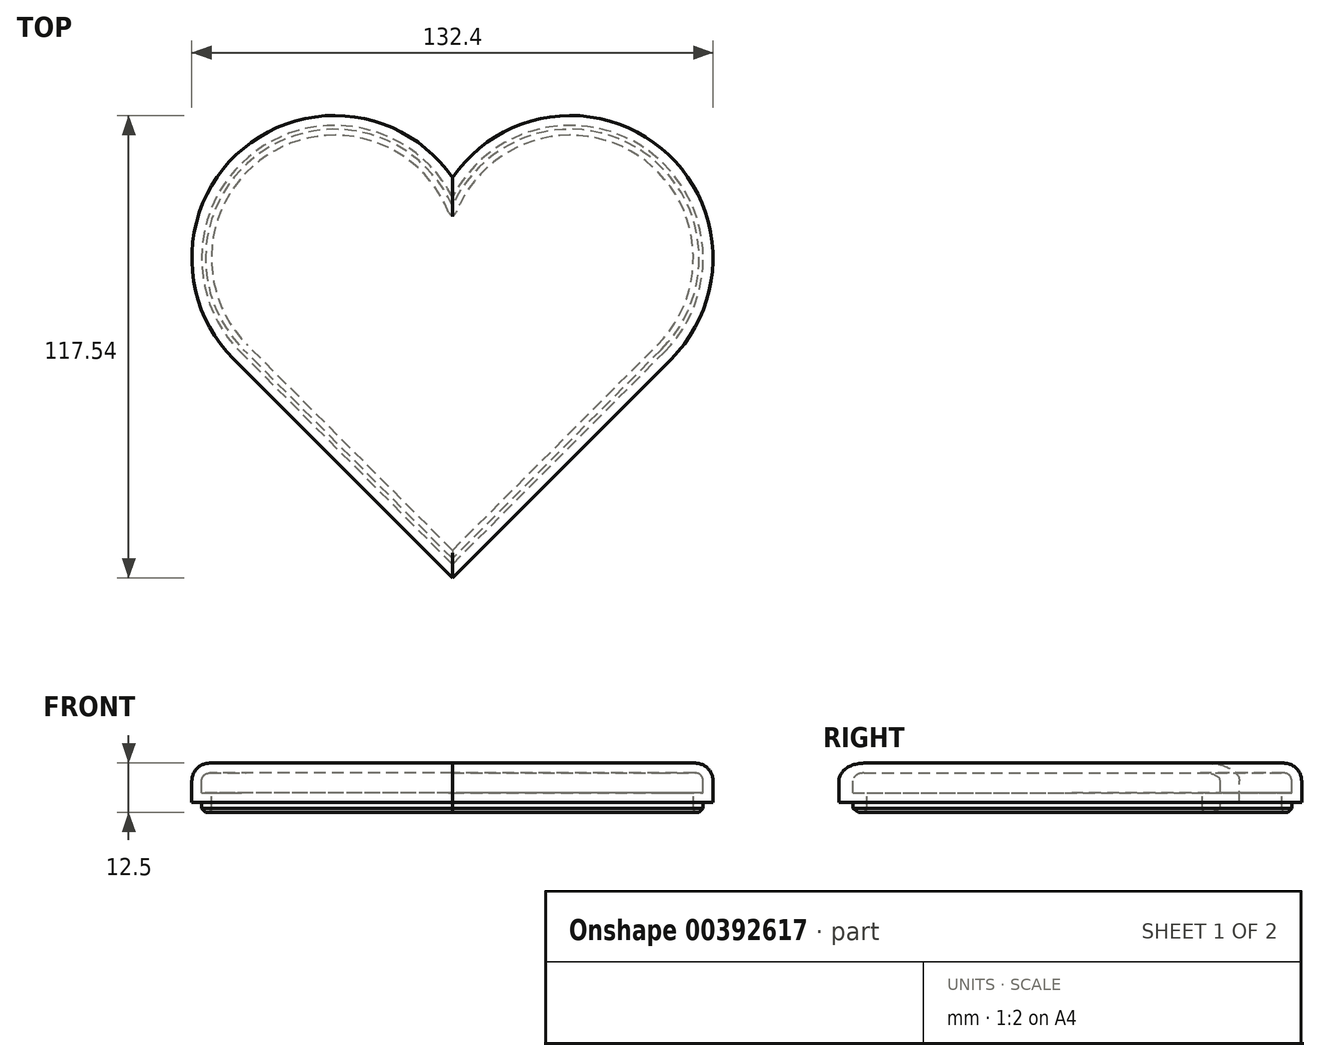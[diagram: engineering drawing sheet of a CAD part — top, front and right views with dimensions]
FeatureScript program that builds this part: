
annotation { "Feature Type Name" : "Feature", "Feature Type Description" : "" }
export const myFeature = defineFeature(function(context is Context, id is Id, definition is map)
    precondition{}
    {
        {
            var Q0;
            Q0=qCreatedBy(makeId("Top.planeOp"),FACE);
            var sketch = newSketch(context, id + "F0", { "sketchPlane" : qUnion([Q0])});
            skLineSegment(sketch, "E0", {"start": v(0, -53.9) * mm, "end": v(53.83, 0) * mm});
            skArc(sketch, "E1", {"start": v(53.83, 0) * mm, "mid": v(49.9, 51.09) * mm, "end": v(0, 39.44) * mm});
            skLineSegment(sketch, "E2", {"start": v(0, -53.9) * mm, "end": v(-53.83, 0) * mm});
            skArc(sketch, "E3", {"start": v(-53.83, 0) * mm, "mid": v(-49.9, 51.09) * mm, "end": v(0, 39.44) * mm});
            skSolve(sketch);
        }
        {
            var Q0;
            Q0=makeQuery(id+"F0.imprint","IMPRINT",FACE,{"disambiguationData":[TD([[makeQuery(id+"F0.imprint","IMPRINT",EDGE,{"derivedFrom":sQuery(id+"F0.wireOp",EDGE,"E0")}),1.0]])]});
            extrude(context, id + "F1", {"entities" : qUnion([Q0]), "oppositeDirection" : true, "depth" : 5 * mm});
        }
        {
            var Q0;
            Q0=makeQuery(id+"F1.opExtrude","CAP_EDGE",EDGE,{"disambiguationData":[OSD([sQuery(id+"F0.wireOp",EDGE,"E0")])],"isStart":true});
            var Q1;
            Q1=makeQuery(id+"F1.opExtrude","CAP_EDGE",EDGE,{"disambiguationData":[OSD([sQuery(id+"F0.wireOp",EDGE,"E2")])],"isStart":true});
            var Q2;
            Q2=makeQuery(id+"F1.opExtrude","CAP_EDGE",EDGE,{"disambiguationData":[OSD([sQuery(id+"F0.wireOp",EDGE,"E3")])],"isStart":true});
            var Q3;
            Q3=makeQuery(id+"F1.opExtrude","CAP_EDGE",EDGE,{"disambiguationData":[OSD([sQuery(id+"F0.wireOp",EDGE,"E1")])],"isStart":true});
            fillet(context, id + "F2", {"entities" : qUnion([Q0, Q1, Q2, Q3]), "radius" : 2 * mm, "tangentPropagation" : true, "allowEdgeOverflow" : false});
        }
        {
            var Q0;
            Q0=makeQuery(id+"F1.opExtrude","CAP_FACE",FACE,{"disambiguationData":[OSD([sQuery(id+"F0.wireOp",EDGE,"E0"),sQuery(id+"F0.wireOp",EDGE,"E1"),sQuery(id+"F0.wireOp",EDGE,"E2"),sQuery(id+"F0.wireOp",EDGE,"E3")])],"isStart":false});
            shell(context, id + "F3", {"entities" : qUnion([Q0]), "thickness" : 2.5 * mm});
        }
        {
            var Q0;
            Q0=makeQuery(id+"F3.opShell","OFFSET_FACE",FACE,{"disambiguationData":[OSD([sQuery(id+"F0.wireOp",EDGE,"E0"),sQuery(id+"F0.wireOp",EDGE,"E1"),sQuery(id+"F0.wireOp",EDGE,"E2"),sQuery(id+"F0.wireOp",EDGE,"E3")])]});
            extrude(context, id + "F4", {"entities" : qUnion([Q0]), "operationType" : NewBodyOperationType.ADD, "depth" : 7.5 * mm});
        }
        {
            var Q0;
            {var subQ0=sQuery(id+"F0.wireOp",EDGE,"E2");var subQ1=makeQuery(id+"F1.opExtrude","CAP_EDGE",EDGE,{"disambiguationData":[OSD([subQ0])],"isStart":true});var subQ2=sQuery(id+"F0.wireOp",EDGE,"E3");var subQ3=sQuery(id+"F0.wireOp",EDGE,"E1");var subQ4=sQuery(id+"F0.wireOp",EDGE,"E0");Q0=makeQuery(id+"F4.opExtrude","CAP_EDGE",EDGE,{"disambiguationData":[OSD([subQ4,subQ3,subQ0,subQ2]),TDD([makeQuery(id+"F3.opShell","OFFSET_EDGE",EDGE,{"disambiguationData":[OSD([subQ4,subQ3,subQ0,subQ2]),TDD([makeQuery(id+"F2.opFillet","BLEND_EDGE",EDGE,{"blendedFrom":[subQ1,makeQuery(id+"F1.opExtrude","CAP_FACE",FACE,{"disambiguationData":[OSD([subQ4,subQ3,subQ0,subQ2])],"isStart":true})],"blendedInto":[makeQuery(id+"F1.opExtrude","CAP_FACE",FACE,{"disambiguationData":[OSD([subQ4,subQ3,subQ0,subQ2])],"isStart":true})]}),makeQuery(id+"F2.opFillet","BLEND_EDGE",EDGE,{"blendedFrom":[subQ1,makeQuery(id+"F1.opExtrude","SWEPT_FACE",FACE,{"disambiguationData":[OSD([subQ0])]})],"blendedInto":[makeQuery(id+"F1.opExtrude","SWEPT_FACE",FACE,{"disambiguationData":[OSD([subQ0])]})]})])]})])],"isStart":false});}
            var Q1;
            {var subQ0=sQuery(id+"F0.wireOp",EDGE,"E3");var subQ1=makeQuery(id+"F1.opExtrude","CAP_EDGE",EDGE,{"disambiguationData":[OSD([subQ0])],"isStart":true});var subQ2=sQuery(id+"F0.wireOp",EDGE,"E2");var subQ3=sQuery(id+"F0.wireOp",EDGE,"E1");var subQ4=sQuery(id+"F0.wireOp",EDGE,"E0");Q1=makeQuery(id+"F4.opExtrude","CAP_EDGE",EDGE,{"disambiguationData":[OSD([subQ4,subQ3,subQ2,subQ0]),TDD([makeQuery(id+"F3.opShell","OFFSET_EDGE",EDGE,{"disambiguationData":[OSD([subQ4,subQ3,subQ2,subQ0]),TDD([makeQuery(id+"F2.opFillet","BLEND_EDGE",EDGE,{"blendedFrom":[subQ1,makeQuery(id+"F1.opExtrude","CAP_FACE",FACE,{"disambiguationData":[OSD([subQ4,subQ3,subQ2,subQ0])],"isStart":true})],"blendedInto":[makeQuery(id+"F1.opExtrude","CAP_FACE",FACE,{"disambiguationData":[OSD([subQ4,subQ3,subQ2,subQ0])],"isStart":true})]}),makeQuery(id+"F2.opFillet","BLEND_EDGE",EDGE,{"blendedFrom":[subQ1,makeQuery(id+"F1.opExtrude","SWEPT_FACE",FACE,{"disambiguationData":[OSD([subQ0])]})],"blendedInto":[makeQuery(id+"F1.opExtrude","SWEPT_FACE",FACE,{"disambiguationData":[OSD([subQ0])]})]})])]})])],"isStart":false});}
            var Q2;
            {var subQ0=sQuery(id+"F0.wireOp",EDGE,"E1");var subQ1=makeQuery(id+"F1.opExtrude","CAP_EDGE",EDGE,{"disambiguationData":[OSD([subQ0])],"isStart":true});var subQ2=sQuery(id+"F0.wireOp",EDGE,"E3");var subQ3=sQuery(id+"F0.wireOp",EDGE,"E2");var subQ4=sQuery(id+"F0.wireOp",EDGE,"E0");Q2=makeQuery(id+"F4.opExtrude","CAP_EDGE",EDGE,{"disambiguationData":[OSD([subQ4,subQ0,subQ3,subQ2]),TDD([makeQuery(id+"F3.opShell","OFFSET_EDGE",EDGE,{"disambiguationData":[OSD([subQ4,subQ0,subQ3,subQ2]),TDD([makeQuery(id+"F2.opFillet","BLEND_EDGE",EDGE,{"blendedFrom":[subQ1,makeQuery(id+"F1.opExtrude","CAP_FACE",FACE,{"disambiguationData":[OSD([subQ4,subQ0,subQ3,subQ2])],"isStart":true})],"blendedInto":[makeQuery(id+"F1.opExtrude","CAP_FACE",FACE,{"disambiguationData":[OSD([subQ4,subQ0,subQ3,subQ2])],"isStart":true})]}),makeQuery(id+"F2.opFillet","BLEND_EDGE",EDGE,{"blendedFrom":[subQ1,makeQuery(id+"F1.opExtrude","SWEPT_FACE",FACE,{"disambiguationData":[OSD([subQ0])]})],"blendedInto":[makeQuery(id+"F1.opExtrude","SWEPT_FACE",FACE,{"disambiguationData":[OSD([subQ0])]})]})])]})])],"isStart":false});}
            var Q3;
            {var subQ0=sQuery(id+"F0.wireOp",EDGE,"E3");var subQ1=sQuery(id+"F0.wireOp",EDGE,"E2");var subQ2=sQuery(id+"F0.wireOp",EDGE,"E1");var subQ3=sQuery(id+"F0.wireOp",EDGE,"E0");var subQ4=makeQuery(id+"F1.opExtrude","CAP_EDGE",EDGE,{"disambiguationData":[OSD([subQ3])],"isStart":true});Q3=makeQuery(id+"F4.opExtrude","CAP_EDGE",EDGE,{"disambiguationData":[OSD([subQ3,subQ2,subQ1,subQ0]),TDD([makeQuery(id+"F3.opShell","OFFSET_EDGE",EDGE,{"disambiguationData":[OSD([subQ3,subQ2,subQ1,subQ0]),TDD([makeQuery(id+"F2.opFillet","BLEND_EDGE",EDGE,{"blendedFrom":[subQ4,makeQuery(id+"F1.opExtrude","SWEPT_FACE",FACE,{"disambiguationData":[OSD([subQ3])]})],"blendedInto":[makeQuery(id+"F1.opExtrude","SWEPT_FACE",FACE,{"disambiguationData":[OSD([subQ3])]})]}),makeQuery(id+"F2.opFillet","BLEND_EDGE",EDGE,{"blendedFrom":[subQ4,makeQuery(id+"F1.opExtrude","CAP_FACE",FACE,{"disambiguationData":[OSD([subQ3,subQ2,subQ1,subQ0])],"isStart":true})],"blendedInto":[makeQuery(id+"F1.opExtrude","CAP_FACE",FACE,{"disambiguationData":[OSD([subQ3,subQ2,subQ1,subQ0])],"isStart":true})]})])]})])],"isStart":false});}
            chamfer(context, id + "F5", {"entities" : qUnion([Q0, Q1, Q2, Q3]), "width" : 1 * mm, "tangentPropagation" : true});
        }
        {
            var Q0;
            Q0=makeQuery(id+"F4.opExtrude","CAP_FACE",FACE,{"disambiguationData":[OSD([sQuery(id+"F0.wireOp",EDGE,"E0"),sQuery(id+"F0.wireOp",EDGE,"E1"),sQuery(id+"F0.wireOp",EDGE,"E2"),sQuery(id+"F0.wireOp",EDGE,"E3")])],"isStart":false});
            shell(context, id + "F6", {"entities" : qUnion([Q0]), "thickness" : 2.5 * mm, "oppositeDirection" : true});
        }
        {
            var Q0;
            {var subQ0=sQuery(id+"F0.wireOp",EDGE,"E2");var subQ1=makeQuery(id+"F1.opExtrude","CAP_EDGE",EDGE,{"disambiguationData":[OSD([subQ0])],"isStart":true});var subQ2=sQuery(id+"F0.wireOp",EDGE,"E3");var subQ3=sQuery(id+"F0.wireOp",EDGE,"E1");var subQ4=sQuery(id+"F0.wireOp",EDGE,"E0");Q0=makeQuery(id+"F6.opShell","TWEAK_EDGE",EDGE,{"derivedFrom":[makeQuery(id+"F4.opExtrude","CAP_FACE",FACE,{"disambiguationData":[OSD([subQ4,subQ3,subQ0,subQ2])],"isStart":false}),makeQuery(id+"F4.opExtrude","SWEPT_FACE",FACE,{"disambiguationData":[OSD([subQ4,subQ3,subQ0,subQ2]),TDD([makeQuery(id+"F3.opShell","OFFSET_EDGE",EDGE,{"disambiguationData":[OSD([subQ4,subQ3,subQ0,subQ2]),TDD([makeQuery(id+"F2.opFillet","BLEND_EDGE",EDGE,{"blendedFrom":[subQ1,makeQuery(id+"F1.opExtrude","CAP_FACE",FACE,{"disambiguationData":[OSD([subQ4,subQ3,subQ0,subQ2])],"isStart":true})],"blendedInto":[makeQuery(id+"F1.opExtrude","CAP_FACE",FACE,{"disambiguationData":[OSD([subQ4,subQ3,subQ0,subQ2])],"isStart":true})]}),makeQuery(id+"F2.opFillet","BLEND_EDGE",EDGE,{"blendedFrom":[subQ1,makeQuery(id+"F1.opExtrude","SWEPT_FACE",FACE,{"disambiguationData":[OSD([subQ0])]})],"blendedInto":[makeQuery(id+"F1.opExtrude","SWEPT_FACE",FACE,{"disambiguationData":[OSD([subQ0])]})]})])]})])]})]});}
            var Q1;
            {var subQ0=sQuery(id+"F0.wireOp",EDGE,"E3");var subQ1=makeQuery(id+"F1.opExtrude","CAP_EDGE",EDGE,{"disambiguationData":[OSD([subQ0])],"isStart":true});var subQ2=sQuery(id+"F0.wireOp",EDGE,"E2");var subQ3=sQuery(id+"F0.wireOp",EDGE,"E1");var subQ4=sQuery(id+"F0.wireOp",EDGE,"E0");Q1=makeQuery(id+"F6.opShell","TWEAK_EDGE",EDGE,{"derivedFrom":[makeQuery(id+"F4.opExtrude","CAP_FACE",FACE,{"disambiguationData":[OSD([subQ4,subQ3,subQ2,subQ0])],"isStart":false}),makeQuery(id+"F4.opExtrude","SWEPT_FACE",FACE,{"disambiguationData":[OSD([subQ4,subQ3,subQ2,subQ0]),TDD([makeQuery(id+"F3.opShell","OFFSET_EDGE",EDGE,{"disambiguationData":[OSD([subQ4,subQ3,subQ2,subQ0]),TDD([makeQuery(id+"F2.opFillet","BLEND_EDGE",EDGE,{"blendedFrom":[subQ1,makeQuery(id+"F1.opExtrude","CAP_FACE",FACE,{"disambiguationData":[OSD([subQ4,subQ3,subQ2,subQ0])],"isStart":true})],"blendedInto":[makeQuery(id+"F1.opExtrude","CAP_FACE",FACE,{"disambiguationData":[OSD([subQ4,subQ3,subQ2,subQ0])],"isStart":true})]}),makeQuery(id+"F2.opFillet","BLEND_EDGE",EDGE,{"blendedFrom":[subQ1,makeQuery(id+"F1.opExtrude","SWEPT_FACE",FACE,{"disambiguationData":[OSD([subQ0])]})],"blendedInto":[makeQuery(id+"F1.opExtrude","SWEPT_FACE",FACE,{"disambiguationData":[OSD([subQ0])]})]})])]})])]})]});}
            var Q2;
            {var subQ0=sQuery(id+"F0.wireOp",EDGE,"E1");var subQ1=makeQuery(id+"F1.opExtrude","CAP_EDGE",EDGE,{"disambiguationData":[OSD([subQ0])],"isStart":true});var subQ2=sQuery(id+"F0.wireOp",EDGE,"E3");var subQ3=sQuery(id+"F0.wireOp",EDGE,"E2");var subQ4=sQuery(id+"F0.wireOp",EDGE,"E0");Q2=makeQuery(id+"F6.opShell","TWEAK_EDGE",EDGE,{"derivedFrom":[makeQuery(id+"F4.opExtrude","CAP_FACE",FACE,{"disambiguationData":[OSD([subQ4,subQ0,subQ3,subQ2])],"isStart":false}),makeQuery(id+"F4.opExtrude","SWEPT_FACE",FACE,{"disambiguationData":[OSD([subQ4,subQ0,subQ3,subQ2]),TDD([makeQuery(id+"F3.opShell","OFFSET_EDGE",EDGE,{"disambiguationData":[OSD([subQ4,subQ0,subQ3,subQ2]),TDD([makeQuery(id+"F2.opFillet","BLEND_EDGE",EDGE,{"blendedFrom":[subQ1,makeQuery(id+"F1.opExtrude","CAP_FACE",FACE,{"disambiguationData":[OSD([subQ4,subQ0,subQ3,subQ2])],"isStart":true})],"blendedInto":[makeQuery(id+"F1.opExtrude","CAP_FACE",FACE,{"disambiguationData":[OSD([subQ4,subQ0,subQ3,subQ2])],"isStart":true})]}),makeQuery(id+"F2.opFillet","BLEND_EDGE",EDGE,{"blendedFrom":[subQ1,makeQuery(id+"F1.opExtrude","SWEPT_FACE",FACE,{"disambiguationData":[OSD([subQ0])]})],"blendedInto":[makeQuery(id+"F1.opExtrude","SWEPT_FACE",FACE,{"disambiguationData":[OSD([subQ0])]})]})])]})])]})]});}
            var Q3;
            {var subQ0=sQuery(id+"F0.wireOp",EDGE,"E3");var subQ1=sQuery(id+"F0.wireOp",EDGE,"E2");var subQ2=sQuery(id+"F0.wireOp",EDGE,"E1");var subQ3=sQuery(id+"F0.wireOp",EDGE,"E0");var subQ4=makeQuery(id+"F1.opExtrude","CAP_EDGE",EDGE,{"disambiguationData":[OSD([subQ3])],"isStart":true});Q3=makeQuery(id+"F6.opShell","TWEAK_EDGE",EDGE,{"derivedFrom":[makeQuery(id+"F4.opExtrude","CAP_FACE",FACE,{"disambiguationData":[OSD([subQ3,subQ2,subQ1,subQ0])],"isStart":false}),makeQuery(id+"F4.opExtrude","SWEPT_FACE",FACE,{"disambiguationData":[OSD([subQ3,subQ2,subQ1,subQ0]),TDD([makeQuery(id+"F3.opShell","OFFSET_EDGE",EDGE,{"disambiguationData":[OSD([subQ3,subQ2,subQ1,subQ0]),TDD([makeQuery(id+"F2.opFillet","BLEND_EDGE",EDGE,{"blendedFrom":[subQ4,makeQuery(id+"F1.opExtrude","SWEPT_FACE",FACE,{"disambiguationData":[OSD([subQ3])]})],"blendedInto":[makeQuery(id+"F1.opExtrude","SWEPT_FACE",FACE,{"disambiguationData":[OSD([subQ3])]})]}),makeQuery(id+"F2.opFillet","BLEND_EDGE",EDGE,{"blendedFrom":[subQ4,makeQuery(id+"F1.opExtrude","CAP_FACE",FACE,{"disambiguationData":[OSD([subQ3,subQ2,subQ1,subQ0])],"isStart":true})],"blendedInto":[makeQuery(id+"F1.opExtrude","CAP_FACE",FACE,{"disambiguationData":[OSD([subQ3,subQ2,subQ1,subQ0])],"isStart":true})]})])]})])]})]});}
            chamfer(context, id + "F7", {"entities" : qUnion([Q0, Q1, Q2, Q3]), "width" : 1 * mm, "tangentPropagation" : true});
        }
        {
            var Q0;
            {var subQ0=sQuery(id+"F0.wireOp",EDGE,"E3");var subQ1=sQuery(id+"F0.wireOp",EDGE,"E2");var subQ2=sQuery(id+"F0.wireOp",EDGE,"E1");var subQ3=sQuery(id+"F0.wireOp",EDGE,"E0");var subQ4=makeQuery(id+"F1.opExtrude","CAP_EDGE",EDGE,{"disambiguationData":[OSD([subQ1])],"isStart":true});Q0=makeQuery(id+"F6.opShell","OFFSET_EDGE",EDGE,{"disambiguationData":[OSD([subQ3,subQ2,subQ1,subQ0]),TDD([makeQuery(id+"F5.opChamfer","BLEND_EDGE",EDGE,{"blendedFrom":[makeQuery(id+"F4.opExtrude","CAP_EDGE",EDGE,{"disambiguationData":[OSD([subQ3,subQ2,subQ1,subQ0]),TDD([makeQuery(id+"F3.opShell","OFFSET_EDGE",EDGE,{"disambiguationData":[OSD([subQ3,subQ2,subQ1,subQ0]),TDD([makeQuery(id+"F2.opFillet","BLEND_EDGE",EDGE,{"blendedFrom":[subQ4,makeQuery(id+"F1.opExtrude","CAP_FACE",FACE,{"disambiguationData":[OSD([subQ3,subQ2,subQ1,subQ0])],"isStart":true})],"blendedInto":[makeQuery(id+"F1.opExtrude","CAP_FACE",FACE,{"disambiguationData":[OSD([subQ3,subQ2,subQ1,subQ0])],"isStart":true})]}),makeQuery(id+"F2.opFillet","BLEND_EDGE",EDGE,{"blendedFrom":[subQ4,makeQuery(id+"F1.opExtrude","SWEPT_FACE",FACE,{"disambiguationData":[OSD([subQ1])]})],"blendedInto":[makeQuery(id+"F1.opExtrude","SWEPT_FACE",FACE,{"disambiguationData":[OSD([subQ1])]})]})])]})])],"isStart":false}),makeQuery(id+"F4.opExtrude","CAP_FACE",FACE,{"disambiguationData":[OSD([subQ3,subQ2,subQ1,subQ0])],"isStart":false})],"blendedInto":[makeQuery(id+"F4.opExtrude","CAP_FACE",FACE,{"disambiguationData":[OSD([subQ3,subQ2,subQ1,subQ0])],"isStart":false})]})])]});}
            var Q1;
            {var subQ0=sQuery(id+"F0.wireOp",EDGE,"E3");var subQ1=sQuery(id+"F0.wireOp",EDGE,"E2");var subQ2=sQuery(id+"F0.wireOp",EDGE,"E1");var subQ3=sQuery(id+"F0.wireOp",EDGE,"E0");var subQ4=makeQuery(id+"F1.opExtrude","CAP_EDGE",EDGE,{"disambiguationData":[OSD([subQ3])],"isStart":true});Q1=makeQuery(id+"F6.opShell","OFFSET_EDGE",EDGE,{"disambiguationData":[OSD([subQ3,subQ2,subQ1,subQ0]),TDD([makeQuery(id+"F5.opChamfer","BLEND_EDGE",EDGE,{"blendedFrom":[makeQuery(id+"F4.opExtrude","CAP_EDGE",EDGE,{"disambiguationData":[OSD([subQ3,subQ2,subQ1,subQ0]),TDD([makeQuery(id+"F3.opShell","OFFSET_EDGE",EDGE,{"disambiguationData":[OSD([subQ3,subQ2,subQ1,subQ0]),TDD([makeQuery(id+"F2.opFillet","BLEND_EDGE",EDGE,{"blendedFrom":[subQ4,makeQuery(id+"F1.opExtrude","SWEPT_FACE",FACE,{"disambiguationData":[OSD([subQ3])]})],"blendedInto":[makeQuery(id+"F1.opExtrude","SWEPT_FACE",FACE,{"disambiguationData":[OSD([subQ3])]})]}),makeQuery(id+"F2.opFillet","BLEND_EDGE",EDGE,{"blendedFrom":[subQ4,makeQuery(id+"F1.opExtrude","CAP_FACE",FACE,{"disambiguationData":[OSD([subQ3,subQ2,subQ1,subQ0])],"isStart":true})],"blendedInto":[makeQuery(id+"F1.opExtrude","CAP_FACE",FACE,{"disambiguationData":[OSD([subQ3,subQ2,subQ1,subQ0])],"isStart":true})]})])]})])],"isStart":false}),makeQuery(id+"F4.opExtrude","CAP_FACE",FACE,{"disambiguationData":[OSD([subQ3,subQ2,subQ1,subQ0])],"isStart":false})],"blendedInto":[makeQuery(id+"F4.opExtrude","CAP_FACE",FACE,{"disambiguationData":[OSD([subQ3,subQ2,subQ1,subQ0])],"isStart":false})]})])]});}
            var Q2;
            {var subQ0=sQuery(id+"F0.wireOp",EDGE,"E3");var subQ1=sQuery(id+"F0.wireOp",EDGE,"E2");var subQ2=sQuery(id+"F0.wireOp",EDGE,"E1");var subQ3=sQuery(id+"F0.wireOp",EDGE,"E0");var subQ4=makeQuery(id+"F1.opExtrude","CAP_EDGE",EDGE,{"disambiguationData":[OSD([subQ0])],"isStart":true});Q2=makeQuery(id+"F6.opShell","OFFSET_EDGE",EDGE,{"disambiguationData":[OSD([subQ3,subQ2,subQ1,subQ0]),TDD([makeQuery(id+"F5.opChamfer","BLEND_EDGE",EDGE,{"blendedFrom":[makeQuery(id+"F4.opExtrude","CAP_EDGE",EDGE,{"disambiguationData":[OSD([subQ3,subQ2,subQ1,subQ0]),TDD([makeQuery(id+"F3.opShell","OFFSET_EDGE",EDGE,{"disambiguationData":[OSD([subQ3,subQ2,subQ1,subQ0]),TDD([makeQuery(id+"F2.opFillet","BLEND_EDGE",EDGE,{"blendedFrom":[subQ4,makeQuery(id+"F1.opExtrude","CAP_FACE",FACE,{"disambiguationData":[OSD([subQ3,subQ2,subQ1,subQ0])],"isStart":true})],"blendedInto":[makeQuery(id+"F1.opExtrude","CAP_FACE",FACE,{"disambiguationData":[OSD([subQ3,subQ2,subQ1,subQ0])],"isStart":true})]}),makeQuery(id+"F2.opFillet","BLEND_EDGE",EDGE,{"blendedFrom":[subQ4,makeQuery(id+"F1.opExtrude","SWEPT_FACE",FACE,{"disambiguationData":[OSD([subQ0])]})],"blendedInto":[makeQuery(id+"F1.opExtrude","SWEPT_FACE",FACE,{"disambiguationData":[OSD([subQ0])]})]})])]})])],"isStart":false}),makeQuery(id+"F4.opExtrude","CAP_FACE",FACE,{"disambiguationData":[OSD([subQ3,subQ2,subQ1,subQ0])],"isStart":false})],"blendedInto":[makeQuery(id+"F4.opExtrude","CAP_FACE",FACE,{"disambiguationData":[OSD([subQ3,subQ2,subQ1,subQ0])],"isStart":false})]})])]});}
            var Q3;
            {var subQ0=sQuery(id+"F0.wireOp",EDGE,"E3");var subQ1=sQuery(id+"F0.wireOp",EDGE,"E2");var subQ2=sQuery(id+"F0.wireOp",EDGE,"E1");var subQ3=sQuery(id+"F0.wireOp",EDGE,"E0");var subQ4=makeQuery(id+"F1.opExtrude","CAP_EDGE",EDGE,{"disambiguationData":[OSD([subQ2])],"isStart":true});Q3=makeQuery(id+"F6.opShell","OFFSET_EDGE",EDGE,{"disambiguationData":[OSD([subQ3,subQ2,subQ1,subQ0]),TDD([makeQuery(id+"F5.opChamfer","BLEND_EDGE",EDGE,{"blendedFrom":[makeQuery(id+"F4.opExtrude","CAP_EDGE",EDGE,{"disambiguationData":[OSD([subQ3,subQ2,subQ1,subQ0]),TDD([makeQuery(id+"F3.opShell","OFFSET_EDGE",EDGE,{"disambiguationData":[OSD([subQ3,subQ2,subQ1,subQ0]),TDD([makeQuery(id+"F2.opFillet","BLEND_EDGE",EDGE,{"blendedFrom":[subQ4,makeQuery(id+"F1.opExtrude","CAP_FACE",FACE,{"disambiguationData":[OSD([subQ3,subQ2,subQ1,subQ0])],"isStart":true})],"blendedInto":[makeQuery(id+"F1.opExtrude","CAP_FACE",FACE,{"disambiguationData":[OSD([subQ3,subQ2,subQ1,subQ0])],"isStart":true})]}),makeQuery(id+"F2.opFillet","BLEND_EDGE",EDGE,{"blendedFrom":[subQ4,makeQuery(id+"F1.opExtrude","SWEPT_FACE",FACE,{"disambiguationData":[OSD([subQ2])]})],"blendedInto":[makeQuery(id+"F1.opExtrude","SWEPT_FACE",FACE,{"disambiguationData":[OSD([subQ2])]})]})])]})])],"isStart":false}),makeQuery(id+"F4.opExtrude","CAP_FACE",FACE,{"disambiguationData":[OSD([subQ3,subQ2,subQ1,subQ0])],"isStart":false})],"blendedInto":[makeQuery(id+"F4.opExtrude","CAP_FACE",FACE,{"disambiguationData":[OSD([subQ3,subQ2,subQ1,subQ0])],"isStart":false})]})])]});}
            fillet(context, id + "F8", {"entities" : qUnion([Q0, Q1, Q2, Q3]), "radius" : 1 * mm, "tangentPropagation" : true, "allowEdgeOverflow" : false});
        }
        {
            var Q0;
            {var subQ0=sQuery(id+"F0.wireOp",EDGE,"E3");var subQ1=sQuery(id+"F0.wireOp",EDGE,"E1");var subQ2=makeQuery(id+"F1.opExtrude","CAP_EDGE",EDGE,{"disambiguationData":[OSD([subQ0])],"isStart":true});var subQ3=makeQuery(id+"F1.opExtrude","CAP_EDGE",EDGE,{"disambiguationData":[OSD([subQ1])],"isStart":true});var subQ4=sQuery(id+"F0.wireOp",EDGE,"E2");var subQ5=sQuery(id+"F0.wireOp",EDGE,"E0");Q0=makeQuery(id+"F6.opShell","OFFSET_EDGE",EDGE,{"disambiguationData":[OSD([subQ5,subQ1,subQ4,subQ0]),TDD([makeQuery(id+"F4.opExtrude","SWEPT_EDGE",EDGE,{"disambiguationData":[OSD([subQ5,subQ1,subQ4,subQ0]),TDD([makeQuery(id+"F3.opShell","OFFSET_VERTEX",VERTEX,{"disambiguationData":[OSD([subQ5,subQ1,subQ4,subQ0]),TDD([makeQuery(id+"F2.opFillet","BLEND_VERTEX",VERTEX,{"blendedFrom":[subQ3,subQ2,makeQuery(id+"F1.opExtrude","CAP_FACE",FACE,{"disambiguationData":[OSD([subQ5,subQ1,subQ4,subQ0])],"isStart":true})],"blendedInto":[makeQuery(id+"F1.opExtrude","CAP_FACE",FACE,{"disambiguationData":[OSD([subQ5,subQ1,subQ4,subQ0])],"isStart":true})]}),makeQuery(id+"F2.opFillet","BLEND_VERTEX",VERTEX,{"blendedFrom":[subQ3,subQ2,makeQuery(id+"F1.opExtrude","SWEPT_FACE",FACE,{"disambiguationData":[OSD([subQ1])]}),makeQuery(id+"F1.opExtrude","SWEPT_FACE",FACE,{"disambiguationData":[OSD([subQ0])]})],"blendedInto":[makeQuery(id+"F1.opExtrude","SWEPT_FACE",FACE,{"disambiguationData":[OSD([subQ1])]}),makeQuery(id+"F1.opExtrude","SWEPT_FACE",FACE,{"disambiguationData":[OSD([subQ0])]})]})])]})])]})])]});}
            fillet(context, id + "F9", {"entities" : qUnion([Q0]), "radius" : 1 * mm, "tangentPropagation" : true, "allowEdgeOverflow" : false});
        }
    });
